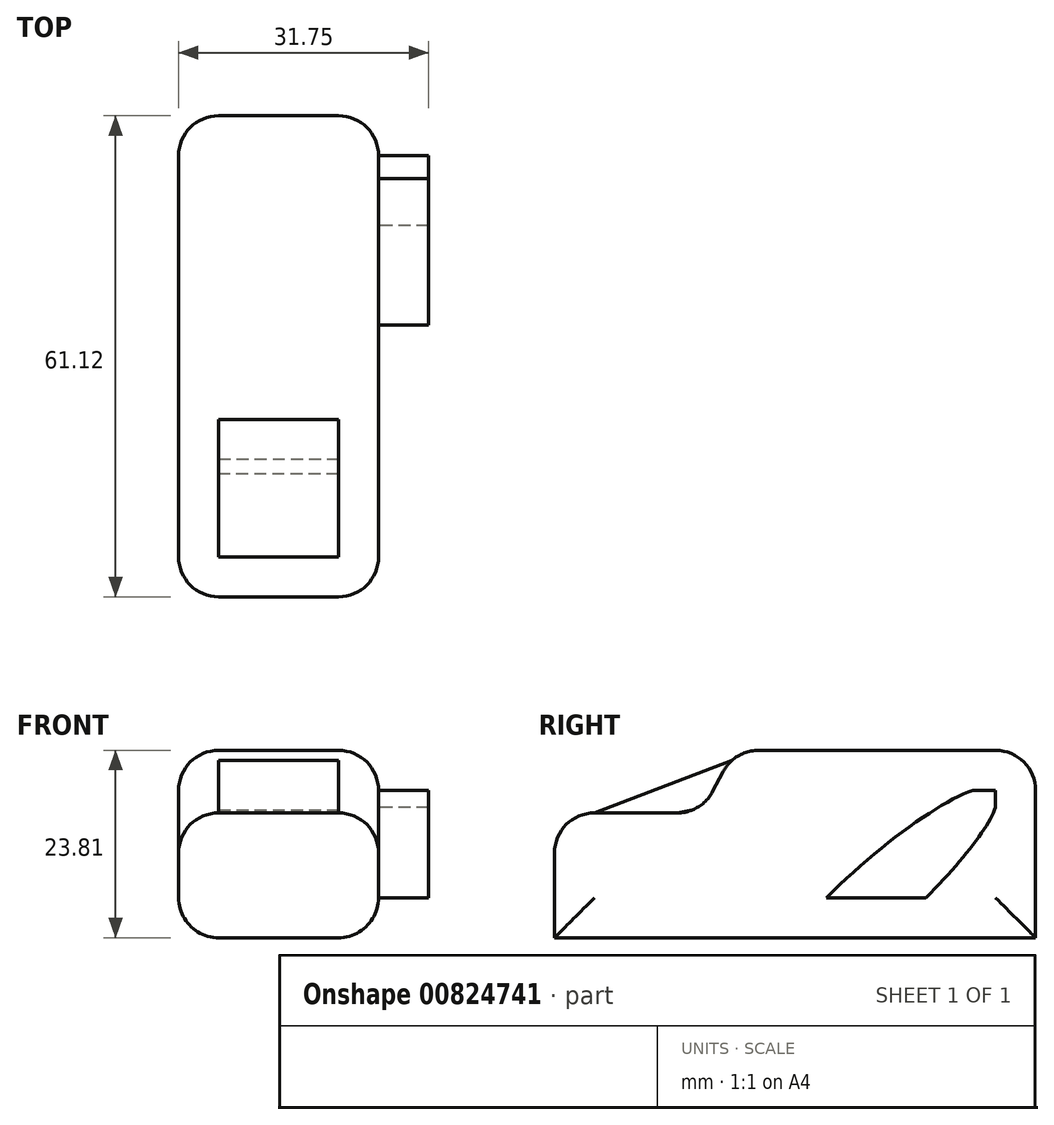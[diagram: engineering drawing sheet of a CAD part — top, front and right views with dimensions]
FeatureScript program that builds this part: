
annotation { "Feature Type Name" : "Feature", "Feature Type Description" : "" }
export const myFeature = defineFeature(function(context is Context, id is Id, definition is map)
    precondition{}
    {
        {
            var Q0;
            Q0=qCreatedBy(makeId("Right.planeOp"),FACE);
            var sketch = newSketch(context, id + "F0", { "sketchPlane" : qUnion([Q0])});
            skLineSegment(sketch, "E0", {"start": v(-56.36, -9.67) * mm, "end": v(-56.36, 6.19) * mm});
            skLineSegment(sketch, "E1", {"start": v(-56.36, 6.19) * mm, "end": v(-37.69, 6.19) * mm});
            skLineSegment(sketch, "E2", {"start": v(-37.69, 6.19) * mm, "end": v(-33.53, 14.14) * mm});
            skLineSegment(sketch, "E3", {"start": v(-33.53, 14.14) * mm, "end": v(4.76, 14.14) * mm});
            skLineSegment(sketch, "E4", {"start": v(4.76, 14.14) * mm, "end": v(4.76, 6.19) * mm});
            skLineSegment(sketch, "E5", {"start": v(4.76, 6.19) * mm, "end": v(4.76, -9.67) * mm});
            skLineSegment(sketch, "E6", {"start": v(4.76, -9.67) * mm, "end": v(-56.36, -9.67) * mm});
            skSolve(sketch);
        }
        {
            var Q0;
            Q0=qSketchRegion(id+"F0",true);
            extrude(context, id + "F1", {"entities" : qUnion([Q0]), "depth" : 25.4 * mm, "offsetDistance" : 25.4 * mm});
        }
        {
            var Q0;
            Q0=makeQuery(id+"F1.opExtrude","CAP_EDGE",EDGE,{"disambiguationData":[OSD([sQuery(id+"F0.wireOp",EDGE,"E0")])],"isStart":false});
            var Q1;
            Q1=makeQuery(id+"F1.opExtrude","SWEPT_EDGE",EDGE,{"disambiguationData":[OSD([sQuery(id+"F0.wireOp",EDGE,"E0"),sQuery(id+"F0.wireOp",EDGE,"E1")])]});
            var Q2;
            Q2=makeQuery(id+"F1.opExtrude","CAP_EDGE",EDGE,{"disambiguationData":[OSD([sQuery(id+"F0.wireOp",EDGE,"E0")])],"isStart":true});
            var Q3;
            Q3=makeQuery(id+"F1.opExtrude","CAP_EDGE",EDGE,{"disambiguationData":[OSD([sQuery(id+"F0.wireOp",EDGE,"E1")])],"isStart":false});
            var Q4;
            Q4=makeQuery(id+"F1.opExtrude","CAP_EDGE",EDGE,{"disambiguationData":[OSD([sQuery(id+"F0.wireOp",EDGE,"E2")])],"isStart":false});
            var Q5;
            Q5=makeQuery(id+"F1.opExtrude","SWEPT_EDGE",EDGE,{"disambiguationData":[OSD([sQuery(id+"F0.wireOp",EDGE,"E2"),sQuery(id+"F0.wireOp",EDGE,"E3")])]});
            var Q6;
            Q6=makeQuery(id+"F1.opExtrude","SWEPT_EDGE",EDGE,{"disambiguationData":[OSD([sQuery(id+"F0.wireOp",EDGE,"E1"),sQuery(id+"F0.wireOp",EDGE,"E2")])]});
            var Q7;
            Q7=makeQuery(id+"F1.opExtrude","CAP_EDGE",EDGE,{"disambiguationData":[OSD([sQuery(id+"F0.wireOp",EDGE,"E3")])],"isStart":false});
            var Q8;
            Q8=makeQuery(id+"F1.opExtrude","CAP_EDGE",EDGE,{"disambiguationData":[OSD([sQuery(id+"F0.wireOp",EDGE,"E3")])],"isStart":true});
            var Q9;
            Q9=makeQuery(id+"F1.opExtrude","SWEPT_EDGE",EDGE,{"disambiguationData":[OSD([sQuery(id+"F0.wireOp",EDGE,"E3"),sQuery(id+"F0.wireOp",EDGE,"E4")])]});
            var Q10;
            Q10=makeQuery(id+"F1.opExtrude","CAP_EDGE",EDGE,{"disambiguationData":[OSD([sQuery(id+"F0.wireOp",EDGE,"E4"),sQuery(id+"F0.wireOp",EDGE,"E5")])],"isStart":false});
            var Q11;
            Q11=makeQuery(id+"F1.opExtrude","CAP_EDGE",EDGE,{"disambiguationData":[OSD([sQuery(id+"F0.wireOp",EDGE,"E6")])],"isStart":false});
            var Q12;
            Q12=makeQuery(id+"F1.opExtrude","CAP_EDGE",EDGE,{"disambiguationData":[OSD([sQuery(id+"F0.wireOp",EDGE,"E4"),sQuery(id+"F0.wireOp",EDGE,"E5")])],"isStart":true});
            var Q13;
            Q13=makeQuery(id+"F1.opExtrude","CAP_EDGE",EDGE,{"disambiguationData":[OSD([sQuery(id+"F0.wireOp",EDGE,"E6")])],"isStart":true});
            var Q14;
            Q14=makeQuery(id+"F1.opExtrude","CAP_EDGE",EDGE,{"disambiguationData":[OSD([sQuery(id+"F0.wireOp",EDGE,"E2")])],"isStart":true});
            var Q15;
            Q15=makeQuery(id+"F1.opExtrude","CAP_EDGE",EDGE,{"disambiguationData":[OSD([sQuery(id+"F0.wireOp",EDGE,"E1")])],"isStart":true});
            fillet(context, id + "F2", {"entities" : qUnion([Q0, Q1, Q2, Q3, Q4, Q5, Q6, Q7, Q8, Q9, Q10, Q11, Q12, Q13, Q14, Q15]), "radius" : 5.08 * mm, "tangentPropagation" : true, "allowEdgeOverflow" : false});
        }
        {
            var Q1;
            Q1=makeQuery(id+"F1.opExtrude","SWEPT_FACE",FACE,{"disambiguationData":[OSD([sQuery(id+"F0.wireOp",EDGE,"E3")])]});
            var Q2;
            Q2=makeQuery(id+"F1.opExtrude","SWEPT_FACE",FACE,{"disambiguationData":[OSD([sQuery(id+"F0.wireOp",EDGE,"E1")])]});
            loft(context, id + "F3", {"operationType" : NewBodyOperationType.ADD, "sheetProfilesArray" : [{ "sheetProfileEntities" : qUnion([Q1]) }, { "sheetProfileEntities" : qUnion([Q2]) }]});
        }
        {
            var Q0;
            Q0=makeQuery(id+"F1.opExtrude","CAP_FACE",FACE,{"disambiguationData":[OSD([sQuery(id+"F0.wireOp",EDGE,"E0"),sQuery(id+"F0.wireOp",EDGE,"E1"),sQuery(id+"F0.wireOp",EDGE,"E2"),sQuery(id+"F0.wireOp",EDGE,"E3"),sQuery(id+"F0.wireOp",EDGE,"E4"),sQuery(id+"F0.wireOp",EDGE,"E5"),sQuery(id+"F0.wireOp",EDGE,"E6")])],"isStart":false});
            var sketch = newSketch(context, id + "F4", { "sketchPlane" : qUnion([Q0])});
            skEllipticalArc(sketch, "E7", {});
            skLineSegment(sketch, "E8", {"start": v(-51.28, -4.6) * mm, "end": v(-0.32, -4.6) * mm});
            skLineSegment(sketch, "E9", {"start": v(-0.32, -4.6) * mm, "end": v(-0.32, 9.06) * mm});
            skLineSegment(sketch, "E10", {"start": v(-0.32, 9.06) * mm, "end": v(-11.6, 9.06) * mm});
            skEllipticalArc(sketch, "E11.trimOffspring", {});
            const initialGuessF4  = {"E7": [-0.015515637584030628, -0.004590079685747623, 0.7440538918741845, 0.6681196045521188, 0.020424407471397815, 0.004337261315943908, 0.46445065350600956, 1.8030216535479], "E11.trimOffspring": [-0.015515637584030628, -0.004590079685747623, 0.7440538918741845, 0.6681196045521188, 0.020424407471397815, 0.004337261315943908, 4.944614307137693, 5.90633981059671]};
            skSetInitialGuess(sketch, initialGuessF4);
            skSolve(sketch);
        }
        {
            var Q0;
            {var subQ4=sQuery(id+"F4.wireOp",EDGE,"E7");Q0=makeQuery(id+"F4.imprint","IMPRINT",FACE,{"disambiguationData":[TD([[makeQuery(id+"F4.imprint","IMPRINT",EDGE,{"derivedFrom":subQ4}),1.0]])]});}
            extrude(context, id + "F5", {"entities" : qUnion([Q0]), "operationType" : NewBodyOperationType.ADD, "depth" : 6.35 * mm, "offsetDistance" : 25.4 * mm});
        }
    });
